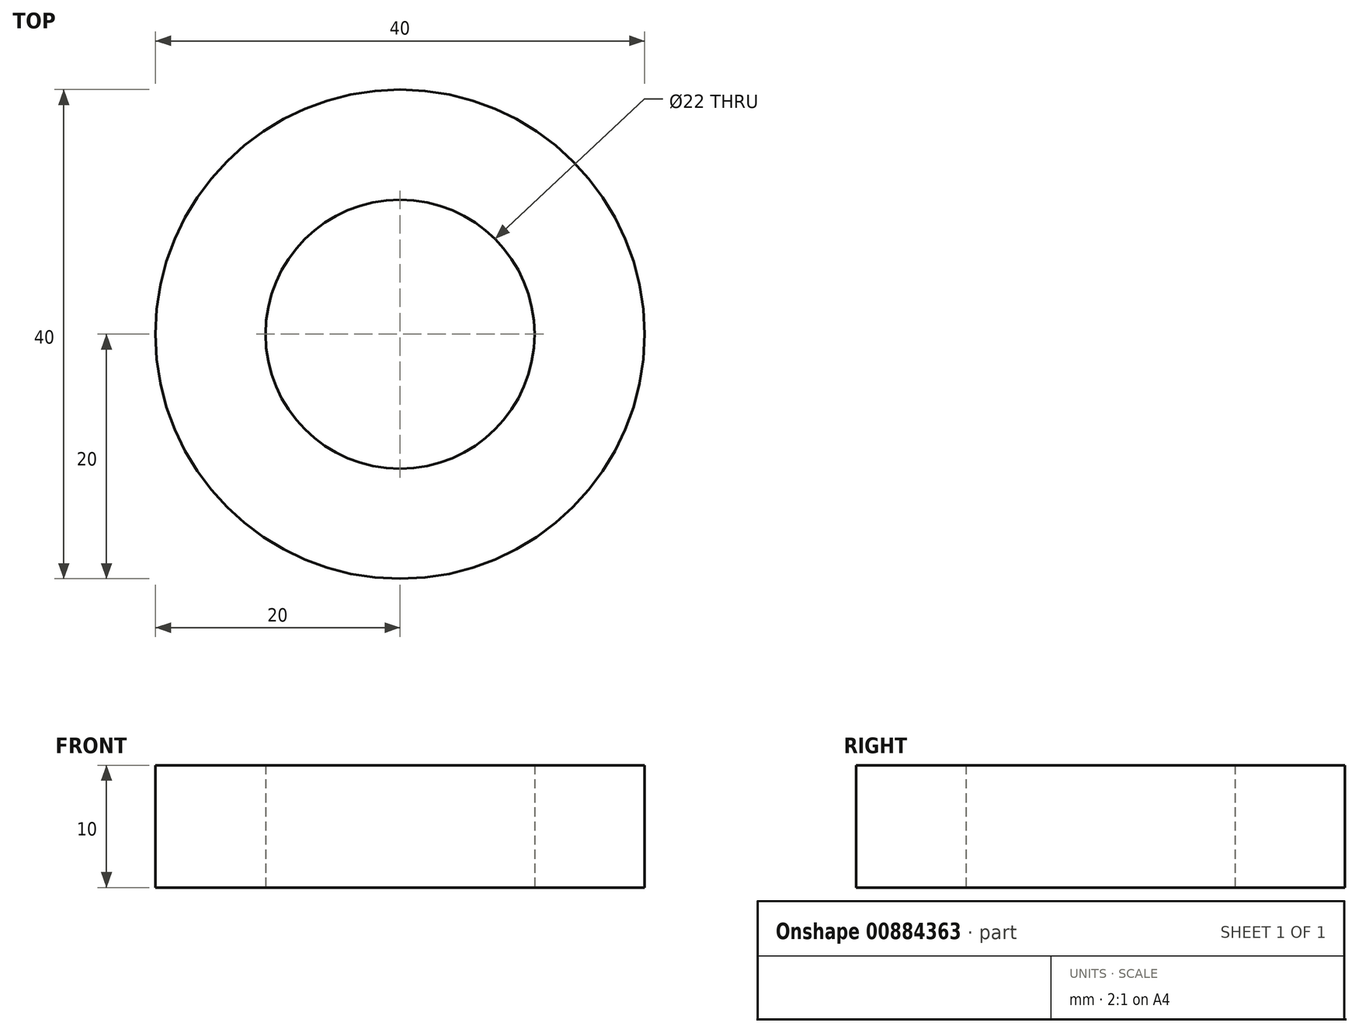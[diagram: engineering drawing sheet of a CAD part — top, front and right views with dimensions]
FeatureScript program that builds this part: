
annotation { "Feature Type Name" : "Feature", "Feature Type Description" : "" }
export const myFeature = defineFeature(function(context is Context, id is Id, definition is map)
    precondition{}
    {
        {
            var Q0;
            Q0=qCreatedBy(makeId("Top.planeOp"),FACE);
            var sketch = newSketch(context, id + "F0", { "sketchPlane" : qUnion([Q0])});
            skCircle(sketch, "E0", {"center": v(0, 0) * mm, "radius": 11 * mm});
            skCircle(sketch, "E1", {"center": v(0, 0) * mm, "radius": 20 * mm});
            skSolve(sketch);
        }
        {
            var Q0;
            Q0 = qSketchRegion(id + "F0", true);
            extrude(context, id + "F1", {"entities" : qUnion([Q0]), "depth" : 10 * mm, "offsetDistance" : 25 * mm});
        }
    });
